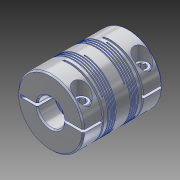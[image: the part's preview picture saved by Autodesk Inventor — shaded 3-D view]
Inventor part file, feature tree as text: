
AUTODESK INVENTOR PART (.ipt)
format: ipt  version: 2015 (Build 190159000, 159)  size: 2,550,784 bytes
history: native  units: in
note: dims shown in document units (in); Inventor stores cm internally (conversion verified against a paired STEP export)
features: imported_body x3, boolean_combine x2, other x1, mirror x1
ambient origin geometry x8: Origin, YZ Plane, XZ Plane, XY Plane, X Axis, Y Axis, Z Axis, Center Point
bodies: Body1 (feature_tree), Body2 (feature_tree), Body3 (feature_tree)
feature tree (7):
  boolean_combine  "Combine3"
  other  "2464K2201"
  mirror  "Mirror1[2]"
  boolean_combine  "Combine4"
  imported_body  "Base1"
  imported_body  "Base2"
  imported_body  "Base3"
